# Revit family: SPB
name_source: partatom
category: Lighting Fixtures
revit_build: Autodesk Revit 2014 (Build: 20130308_1515(x64)
units: mm (PartAtom-declared; Revit-internal decimal feet)

## types (1)
- SPB
    Apparent Load = 42 VA
    Assembly Code = D5020200
    Body Material = Paint - Hubbell - Carbon Black
    Color Filter = 16777215
    Default Elevation = 0"
    Description = Architectural Outdoor Lighting
    Dimming Lamp Color Temperature Shift = <None>
    Emit Shape Visible in Rendering = No
    Emit from Circle Diameter = 6"
    Frame Material = Metal-Hubbell-Gray
    Glass Material = Glass-Kim Lighting-Clear
    Grille material = Metal-Hubbell-Bronze
    Lamp = LED/COMPACT FLUORESCENT/METAL HALIDE/HIGH PRESSURE SODIUM
    Load Classification = Lighting
    Manufacturer = Architectural Area Lighting
    MasterFormat Title = Parking Lighting, Roadway Lighting, Site Lighting
    Model = SPB
    Number of Poles = 1
    OmniClass Number = 23.80.70.14.11.11
    OmniClass Title = Lighting Bollard
    Photometric Notes = More IES files download on Photometric Web Link
    Photometric Web File = SPB.IES
    Photometric Web Link = https://www.hubbell.com
    Power Factor = 1
    Product Documentation Link = https://hubbellcdn.com
    Product Page URL = https://www.hubbell.com
    Series = Spectra Bollard
    Shaft Height = 42"
    Tilt Angle = -90.00°
    Type Comments = Lighting Fixture
    URL = https://www.hubbell.com
    Voltage = 120 V
    Wattage Comments = 42W
    Width = 7 1/2"

## geometry (parser evidence)
native form markers: Blend x8, Sweep x3
no freeform markers — native parametric forms only
